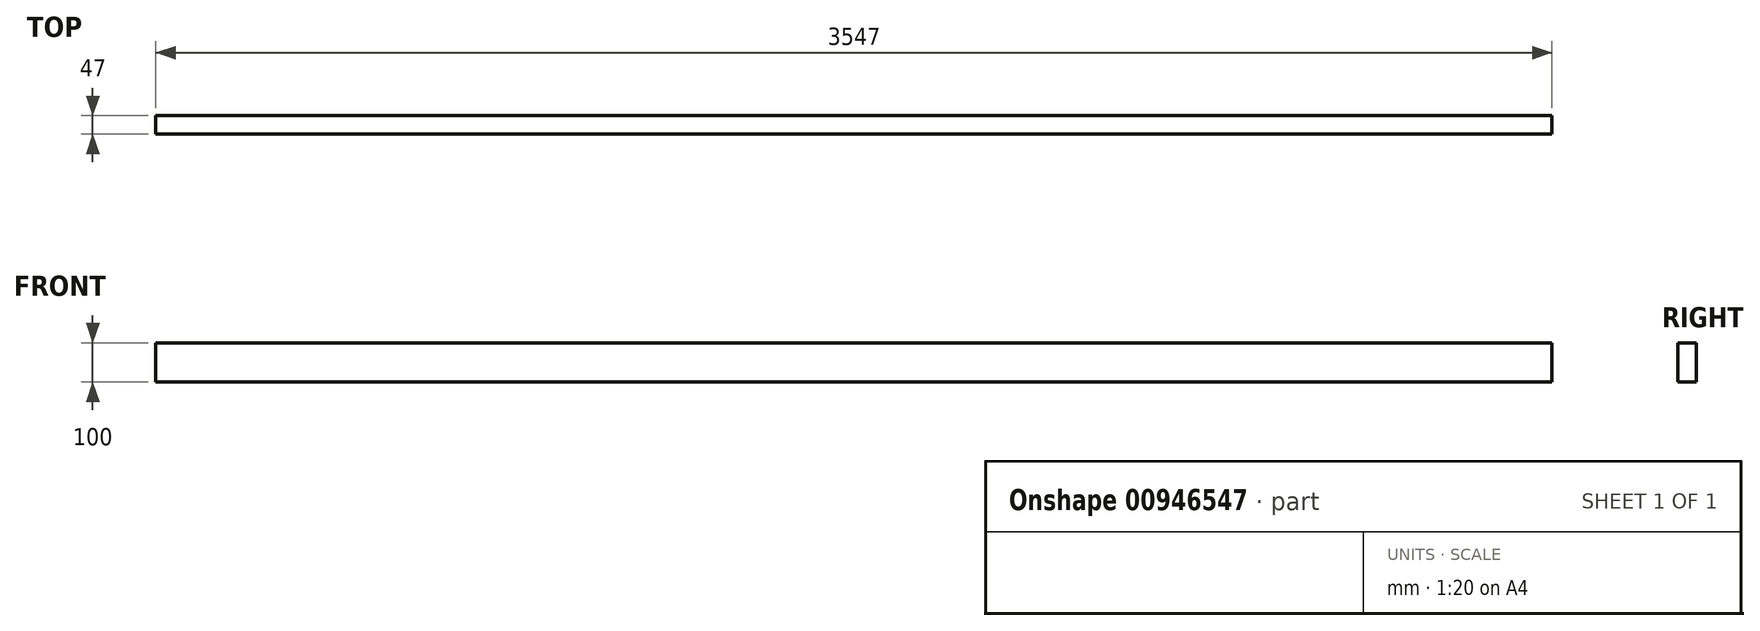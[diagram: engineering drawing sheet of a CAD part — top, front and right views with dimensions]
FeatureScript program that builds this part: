
annotation { "Feature Type Name" : "Feature", "Feature Type Description" : "" }
export const myFeature = defineFeature(function(context is Context, id is Id, definition is map)
    precondition{}
    {
        {
            var Q0;
            Q0=qCreatedBy(makeId("Right.planeOp"),FACE);
            var sketch = newSketch(context, id + "F0", { "sketchPlane" : qUnion([Q0])});
            skLineSegment(sketch, "E0.bottom", {"start": v(0, 0) * mm, "end": v(-47, 0) * mm});
            skLineSegment(sketch, "E0.top", {"start": v(0, 100) * mm, "end": v(-47, 100) * mm});
            skLineSegment(sketch, "E0.left", {"start": v(0, 0) * mm, "end": v(0, 100) * mm});
            skLineSegment(sketch, "E0.right", {"start": v(-47, 0) * mm, "end": v(-47, 100) * mm});
            skSolve(sketch);
        }
        {
            var Q0;
            Q0=qSketchRegion(id+"F0",true);
            extrude(context, id + "F1", {"entities" : qUnion([Q0]), "depth" : 3547 * mm, "offsetDistance" : 25 * mm});
        }
    });
